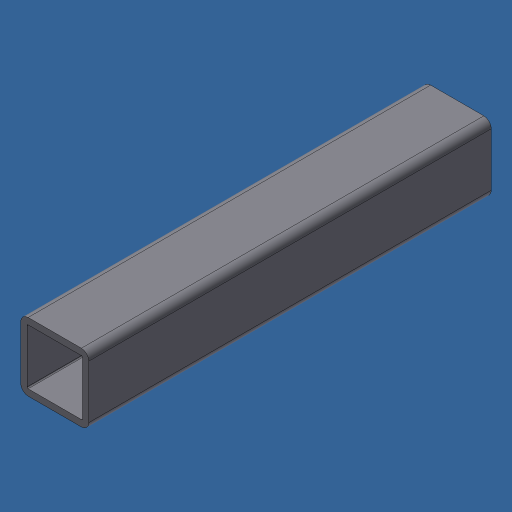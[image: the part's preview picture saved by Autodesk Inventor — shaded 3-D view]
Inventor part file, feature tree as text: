
AUTODESK INVENTOR PART (.ipt)
format: ipt  version: 2024.3 (Build 283343000, 343)  size: 153,600 bytes
history: native  units: mm (DEFAULTED — no unit token found)
features: other x5, extrude x2, fillet x1, shell x1
ambient origin geometry x8: Origin, YZ Plane, XZ Plane, XY Plane, X Axis, Y Axis, Z Axis, Center Point
bodies: Body1 (feature_tree)
feature tree (9):
  other  "Finish - None"
  extrude  "Extrusion1"  TaperAngle=0.0deg  [1 undecoded]
  fillet  "Fillet1"  Radius=25.4mm
  shell  "Shell1"  Thickness=-7.853982mm
  other  "TaperEdge1-YZ"
  other  "TaperEdge2-YZ"
  other  "TaperEdge1-XZ"
  other  "TaperEdge2-XZ"
  extrude  "ForkSlots"  [1 undecoded]
note: 2 required parameter values undecoded (feature->parameter linkage not recoverable at this tier; creation-order binding heuristic only, values carry confidence <= 0.55)
